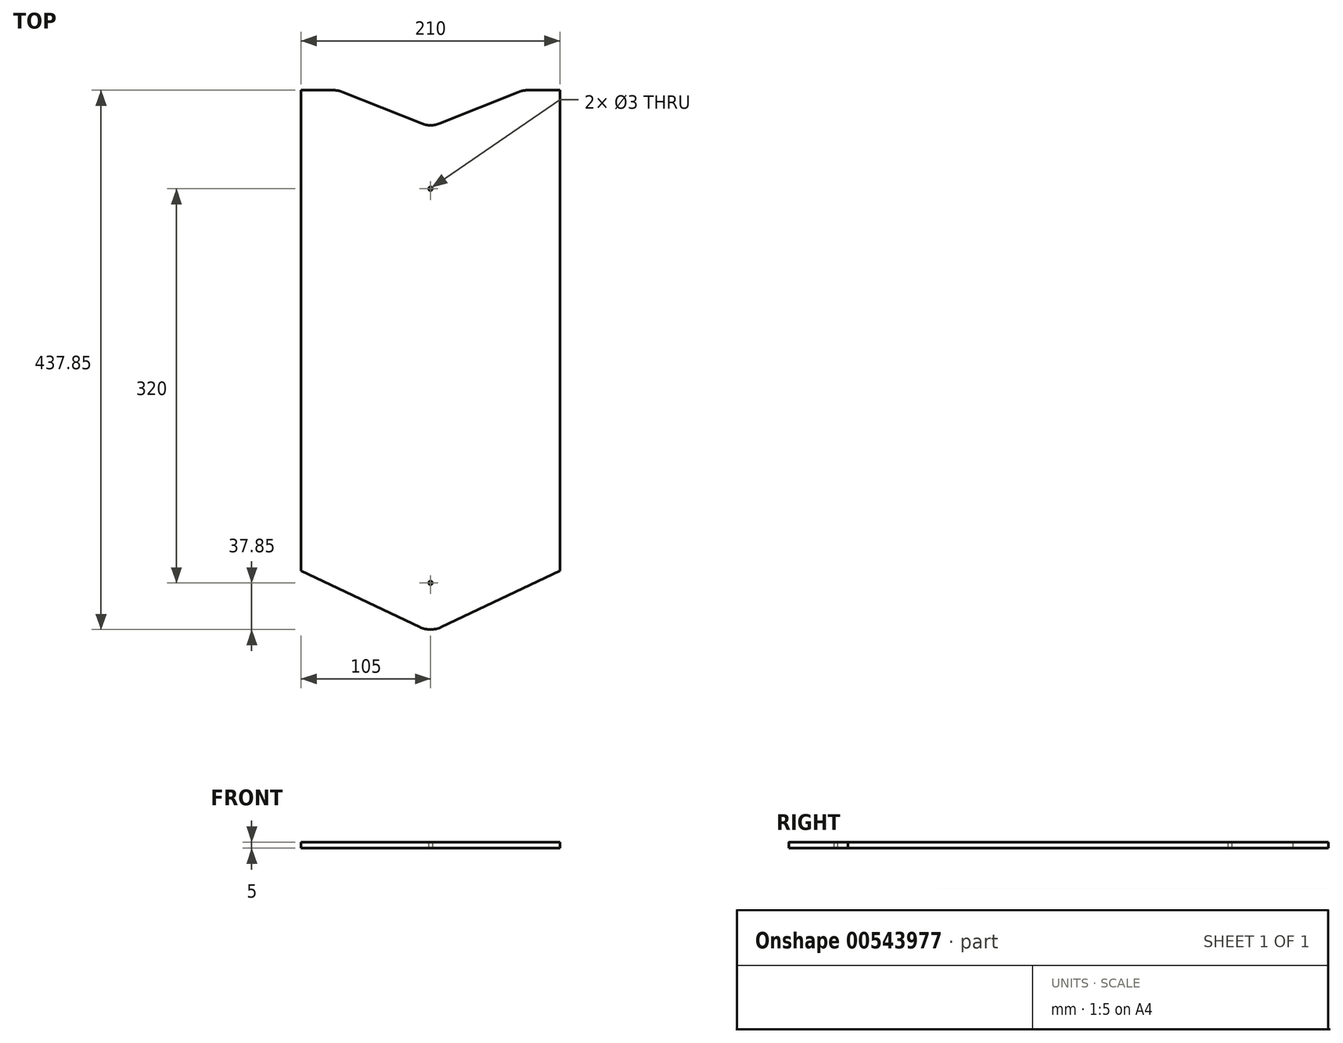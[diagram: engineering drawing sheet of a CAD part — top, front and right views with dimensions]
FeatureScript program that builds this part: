
annotation { "Feature Type Name" : "Feature", "Feature Type Description" : "" }
export const myFeature = defineFeature(function(context is Context, id is Id, definition is map)
    precondition{}
    {
        {
            var Q0;
            Q0=qCreatedBy(makeId("Top.planeOp"),FACE);
            var sketch = newSketch(context, id + "F0", { "sketchPlane" : qUnion([Q0])});
            skLineSegment(sketch, "E0.bottom", {"start": v(0, 0) * mm, "end": v(-105, 0) * mm});
            skLineSegment(sketch, "E0.top", {"start": v(0, 440) * mm, "end": v(-105, 440) * mm});
            skLineSegment(sketch, "E0.left", {"start": v(0, 0) * mm, "end": v(0, 440) * mm});
            skLineSegment(sketch, "E0.right", {"start": v(-105, 0) * mm, "end": v(-105, 440) * mm});
            skLineSegment(sketch, "E1", {"start": v(0, 0) * mm, "end": v(-105, 50) * mm});
            skLineSegment(sketch, "E2", {"start": v(-75, 440) * mm, "end": v(0, 410) * mm});
            skPoint(sketch, "E3", {"position": v(0, 360) * mm});
            skPoint(sketch, "E4", {"position": v(0, 40) * mm});
            skSolve(sketch);
        }
        {
            var Q0;
            {var subQ3=sQuery(id+"F0.wireOp",EDGE,"E1");Q0=makeQuery(id+"F0.imprint","IMPRINT",FACE,{"disambiguationData":[TD([[makeQuery(id+"F0.imprint","IMPRINT",EDGE,{"derivedFrom":subQ3}),-1.0]])]});}
            extrude(context, id + "F1", {"entities" : qUnion([Q0]), "depth" : 5 * mm, "offsetDistance" : 25 * mm});
        }
        {
            var Q0;
            Q0=makeQuery(id+"F1.opExtrude","SWEPT_BODY",BODY,{"disambiguationData":[OSD([sQuery(id+"F0.wireOp",EDGE,"E0.top"),sQuery(id+"F0.wireOp",EDGE,"E0.left"),sQuery(id+"F0.wireOp",EDGE,"E0.right"),sQuery(id+"F0.wireOp",EDGE,"E1"),sQuery(id+"F0.wireOp",EDGE,"E2")])]});
            var Q1;
            Q1=qCreatedBy(makeId("Right.planeOp"),FACE);
            mirror(context, id + "F2", {"operationType" : NewBodyOperationType.ADD, "entities" : qUnion([Q0]), "mirrorPlane" : qUnion([Q1])});
        }
        {
            var Q0;
            {var subQ0=makeQuery(id+"F1.opExtrude","SWEPT_EDGE",EDGE,{"disambiguationData":[OSD([sQuery(id+"F0.wireOp",EDGE,"E0.bottom"),sQuery(id+"F0.wireOp",EDGE,"E0.left"),sQuery(id+"F0.wireOp",EDGE,"E1")])]});Q0=makeQuery(id+"F2.boolean.opBoolean","MERGE",EDGE,{"derivedFrom":[subQ0,makeQuery(id+"F2.opPattern","COPY",EDGE,{"derivedFrom":subQ0,"instanceName":"1"})]});}
            var Q1;
            {var subQ0=makeQuery(id+"F1.opExtrude","SWEPT_EDGE",EDGE,{"disambiguationData":[OSD([sQuery(id+"F0.wireOp",EDGE,"E0.left"),sQuery(id+"F0.wireOp",EDGE,"E2")])]});Q1=makeQuery(id+"F2.boolean.opBoolean","MERGE",EDGE,{"derivedFrom":[subQ0,makeQuery(id+"F2.opPattern","COPY",EDGE,{"derivedFrom":subQ0,"instanceName":"1"})]});}
            var Q2;
            Q2=makeQuery(id+"F2.opPattern","COPY",EDGE,{"derivedFrom":makeQuery(id+"F1.opExtrude","SWEPT_EDGE",EDGE,{"disambiguationData":[OSD([sQuery(id+"F0.wireOp",EDGE,"E0.top"),sQuery(id+"F0.wireOp",EDGE,"E2")])]}),"instanceName":"1"});
            var Q3;
            Q3=makeQuery(id+"F1.opExtrude","SWEPT_EDGE",EDGE,{"disambiguationData":[OSD([sQuery(id+"F0.wireOp",EDGE,"E0.top"),sQuery(id+"F0.wireOp",EDGE,"E2")])]});
            fillet(context, id + "F3", {"entities" : qUnion([Q0, Q1, Q2, Q3]), "radius" : 20 * mm, "tangentPropagation" : true, "allowEdgeOverflow" : false});
        }
        {
            var Q0;
            Q0=sQuery(id+"F0.wireOp",VERTEX,"E3");
            var Q1;
            Q1=sQuery(id+"F0.wireOp",VERTEX,"E4");
            var Q2;
            Q2=makeQuery(id+"F1.opExtrude","SWEPT_BODY",BODY,{"disambiguationData":[OSD([sQuery(id+"F0.wireOp",EDGE,"E0.top"),sQuery(id+"F0.wireOp",EDGE,"E0.left"),sQuery(id+"F0.wireOp",EDGE,"E0.right"),sQuery(id+"F0.wireOp",EDGE,"E1"),sQuery(id+"F0.wireOp",EDGE,"E2")])]});
            hole(context, id + "F4", {"style" : HoleStyle.SIMPLE, "endStyle" : HoleEndStyle.THROUGH, "oppositeDirection" : true, "holeDiameter" : 3 * mm, "isTappedThrough" : true, "tappedDepth" : 12 * mm, "tapClearance" : 3, "locations" : qUnion([Q0, Q1]), "scope" : qUnion([Q2])});
        }
    });
